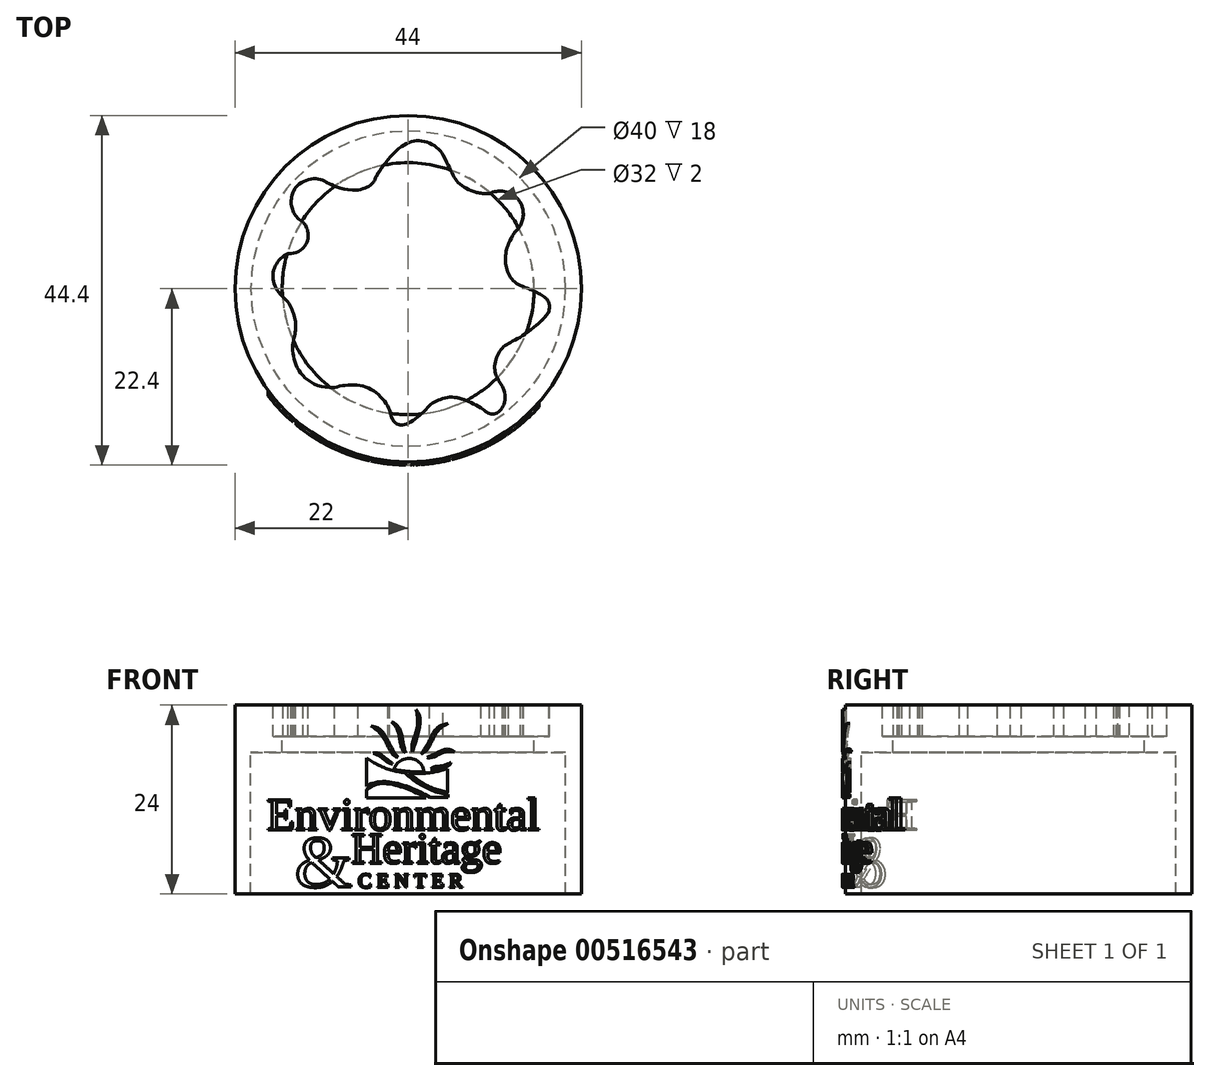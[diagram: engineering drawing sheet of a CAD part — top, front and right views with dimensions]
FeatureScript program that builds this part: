
annotation { "Feature Type Name" : "Feature", "Feature Type Description" : "" }
export const myFeature = defineFeature(function(context is Context, id is Id, definition is map)
    precondition{}
    {
        {
            var Q0;
            Q0=qCreatedBy(makeId("Top.planeOp"),FACE);
            var Q1;
            Q1=qBodyType(qCreatedBy(id+"F1",EDGE),BodyType.WIRE);
            cPlane(context, id + "F0", {"entities" : qUnion([Q0, Q1]), "cplaneType" : CPlaneType.OFFSET, "offset" : 12 * mm, "width" : 150 * mm, "height" : 150 * mm});
        }
        {
            var Q0;
            Q0=qCreatedBy(id+"F0.planeOp",FACE);
            var sketch = newSketch(context, id + "F1", { "sketchPlane" : qUnion([Q0])});
            skCircle(sketch, "E0", {"center": v(0, 0) * mm, "radius": 22 * mm});
            skFitSpline(sketch, "E1", {"points": [v(-14.3, 12.84) * mm, v(-11.44, 13.95) * mm, v(-6.4, 12.53) * mm], "startDerivative": vector(4.46, 5.6) * mm, "endDerivative": vector(16.32, 0.58) * mm});
            skFitSpline(sketch, "E2", {"points": [v(-14.3, 12.84) * mm, v(-14.8, 10.36) * mm, v(-13.38, 8.48) * mm], "startDerivative": vector(-2.91, -3.74) * mm, "endDerivative": vector(4.44, -2.3) * mm});
            skFitSpline(sketch, "E3", {"points": [v(-13.38, 8.48) * mm, v(-12.7, 6.62) * mm, v(-15.26, 4.45) * mm], "startDerivative": vector(2.5, -2.67) * mm, "endDerivative": vector(-9.07, 0.1) * mm});
            skFitSpline(sketch, "E4", {"points": [v(-15.26, 4.45) * mm, v(-17.17, 1.96) * mm, v(-15.87, -1.05) * mm], "startDerivative": vector(-5.88, -2.54) * mm, "endDerivative": vector(5.37, -3.99) * mm});
            skFitSpline(sketch, "E5", {"points": [v(-15.87, -1.05) * mm, v(-14.36, -3.98) * mm, v(-14.54, -6.45) * mm], "startDerivative": vector(4.6, -4.23) * mm, "endDerivative": vector(-1.12, -5.28) * mm});
            skFitSpline(sketch, "E6", {"points": [v(-14.54, -6.45) * mm, v(-14.3, -9.6) * mm, v(-9.38, -12.57) * mm], "startDerivative": vector(-1.49, -4.88) * mm, "endDerivative": vector(14.07, 0.6) * mm});
            skFitSpline(sketch, "E7", {"points": [v(-9.38, -12.57) * mm, v(-5.16, -12.57) * mm, v(-2.36, -15.43) * mm], "startDerivative": vector(7.18, 2.12) * mm, "endDerivative": vector(2.53, -6.19) * mm});
            skFitSpline(sketch, "E8", {"points": [v(-2.36, -15.43) * mm, v(-0.75, -17.32) * mm, v(2.7, -14.82) * mm], "startDerivative": vector(1.67, -9.42) * mm, "endDerivative": vector(5.03, 5.85) * mm});
            skFitSpline(sketch, "E9", {"points": [v(2.7, -14.82) * mm, v(5.45, -13.78) * mm, v(9.22, -15.14) * mm], "startDerivative": vector(4.06, 3.24) * mm, "endDerivative": vector(7.18, -3.93) * mm});
            skFitSpline(sketch, "E10", {"points": [v(9.22, -15.14) * mm, v(11.11, -15.85) * mm, v(12.13, -12.78) * mm], "startDerivative": vector(4.38, -3.77) * mm, "endDerivative": vector(-2.9, 8.35) * mm});
            skFitSpline(sketch, "E11", {"points": [v(12.13, -12.78) * mm, v(11.06, -10.66) * mm, v(11.96, -7.51) * mm], "startDerivative": vector(-1.65, 4.16) * mm, "endDerivative": vector(4.57, 5.25) * mm});
            skFitSpline(sketch, "E12", {"points": [v(11.96, -7.51) * mm, v(14.65, -5.88) * mm, v(17.91, -2.7) * mm], "startDerivative": vector(3.62, 3.57) * mm, "endDerivative": vector(-0.15, 3.1) * mm});
            skFitSpline(sketch, "E13", {"points": [v(17.91, -2.7) * mm, v(16.74, -0.7) * mm, v(14.28, 0.37) * mm], "startDerivative": vector(0.98, 7.59) * mm, "endDerivative": vector(-4.1, 1.2) * mm});
            skFitSpline(sketch, "E14", {"points": [v(14.28, 0.37) * mm, v(12.43, 2.83) * mm, v(12.74, 5.73) * mm], "startDerivative": vector(-6.41, 2.8) * mm, "endDerivative": vector(2.08, 5.38) * mm});
            skFitSpline(sketch, "E15", {"points": [v(12.74, 5.73) * mm, v(14.05, 7.73) * mm, v(14.57, 9.89) * mm], "startDerivative": vector(4.72, 10.1) * mm, "endDerivative": vector(-1.17, 4.74) * mm});
            skFitSpline(sketch, "E16", {"points": [v(14.57, 9.89) * mm, v(13.17, 12.02) * mm, v(10.32, 12.08) * mm], "startDerivative": vector(0.08, 3.85) * mm, "endDerivative": vector(-4.12, -2.28) * mm});
            skFitSpline(sketch, "E17", {"points": [v(10.32, 12.08) * mm, v(6.46, 13.4) * mm, v(4.44, 16.97) * mm], "startDerivative": vector(-9.93, -0.41) * mm, "endDerivative": vector(-5.62, 10.83) * mm});
            skFitSpline(sketch, "E18", {"points": [v(4.44, 16.97) * mm, v(1.52, 18.8) * mm, v(-2.58, 16.4) * mm], "startDerivative": vector(-2.9, 6.35) * mm, "endDerivative": vector(-8.38, -9.56) * mm});
            skFitSpline(sketch, "E19", {"points": [v(-2.58, 16.4) * mm, v(-4.36, 13.61) * mm, v(-6.4, 12.53) * mm], "startDerivative": vector(-9.43, -11.95) * mm, "endDerivative": vector(-8.2, -1.4) * mm});
            skCircle(sketch, "E20", {"center": v(0, 0) * mm, "radius": 20 * mm});
            skSolve(sketch);
        }
        {
            var Q0;
            Q0=qCreatedBy(makeId("Top.planeOp"),FACE);
            cPlane(context, id + "F2", {"entities" : qUnion([Q0]), "cplaneType" : CPlaneType.OFFSET, "offset" : 8 * mm, "width" : 150 * mm, "height" : 150 * mm});
        }
        {
            var Q0;
            Q0=qCreatedBy(id+"F2.planeOp",FACE);
            var sketch = newSketch(context, id + "F3", { "sketchPlane" : qUnion([Q0])});
            skCircle(sketch, "E21", {"center": v(0, 0) * mm, "radius": 20 * mm});
            skCircle(sketch, "E22", {"center": v(0, 0) * mm, "radius": 16 * mm});
            skSolve(sketch);
        }
        {
            var Q0;
            Q0=makeQuery(id+"F1.imprint","IMPRINT",FACE,{"disambiguationData":[TD([[makeQuery(id+"F1.imprint","IMPRINT",EDGE,{"derivedFrom":sQuery(id+"F1.wireOp",EDGE,"E1")}),1.0]])]});
            extrude(context, id + "F4", {"entities" : qUnion([Q0]), "oppositeDirection" : true, "depth" : 4 * mm});
        }
        {
            var Q0;
            Q0=makeQuery(id+"F1.imprint","IMPRINT",FACE,{"disambiguationData":[TD([[makeQuery(id+"F1.imprint","IMPRINT",EDGE,{"derivedFrom":sQuery(id+"F1.wireOp",EDGE,"E0")}),1.0]])]});
            extrude(context, id + "F5", {"entities" : qUnion([Q0]), "operationType" : NewBodyOperationType.ADD, "oppositeDirection" : true, "depth" : 24 * mm});
        }
        {
            var Q0;
            Q0=makeQuery(id+"F3.imprint","IMPRINT",FACE,{"disambiguationData":[TD([[makeQuery(id+"F3.imprint","IMPRINT",EDGE,{"derivedFrom":sQuery(id+"F3.wireOp",EDGE,"E21")}),1.0]])]});
            extrude(context, id + "F6", {"entities" : qUnion([Q0]), "operationType" : NewBodyOperationType.ADD, "oppositeDirection" : true, "depth" : 2 * mm});
        }
        {
            var Q0;
            Q0=qCreatedBy(id+"F0.planeOp",FACE);
            var sketch = newSketch(context, id + "F7", { "sketchPlane" : qUnion([Q0])});
            skCircle(sketch, "E23", {"center": v(0, 0) * mm, "radius": 22.4 * mm});
            skSolve(sketch);
        }
        {
            var Q0;
            Q0=qSketchRegion(id+"F7",true);
            var Q1;
            Q1=qConstructionFilter(qBodyType(qCreatedBy(id+"F7",EDGE),BodyType.WIRE),ConstructionObject.NO);
            extrude(context, id + "F8", {"entities" : qUnion([Q0]), "bodyType" : ToolBodyType.SURFACE, "operationType" : NewBodyOperationType.ADD, "surfaceEntities" : qUnion([Q1]), "oppositeDirection" : true, "depth" : 24 * mm});
        }
        {
            var Q0;
            Q0=qCreatedBy(makeId("Front.planeOp"),FACE);
            var sketch = newSketch(context, id + "F9", { "sketchPlane" : qUnion([Q0])});
            skText(sketch, "E24", { "text": "Environmental", "fontName": "Tinos-Regular.ttf"});
            skText(sketch, "E25", { "text": "Heritage", "fontName": "Tinos-Regular.ttf"});
            skText(sketch, "E26", { "text": "C E N T E R", "fontName": "Tinos-Regular.ttf"});
            skText(sketch, "E27", { "text": "&", "fontName": "Tinos-Regular.ttf"});
            skFitSpline(sketch, "E28", {"points": [v(0.99, 11.47) * mm, v(1.29, 8.55) * mm, v(0.58, 6.04) * mm], "startDerivative": vector(4.15, -4.4) * mm, "endDerivative": vector(-0.93, -4.32) * mm});
            skFitSpline(sketch, "E29", {"points": [v(0.99, 11.47) * mm, v(0.99, 8.58) * mm, v(0.58, 6.04) * mm], "startDerivative": vector(1.84, -7.67) * mm, "endDerivative": vector(1.86, -5.34) * mm});
            skFitSpline(sketch, "E30", {"points": [v(-2.14, 9.9) * mm, v(-0.8, 7.92) * mm, v(-0.37, 5.94) * mm], "startDerivative": vector(6.63, -2.68) * mm, "endDerivative": vector(1.8, -8.41) * mm});
            skFitSpline(sketch, "E31", {"points": [v(-2.14, 9.9) * mm, v(-1.12, 7.92) * mm, v(-0.37, 5.94) * mm], "startDerivative": vector(5.12, -5.44) * mm, "endDerivative": vector(3.25, -2.08) * mm});
            skFitSpline(sketch, "E32", {"points": [v(-4.7, 9.34) * mm, v(-2.58, 7.48) * mm, v(-1.32, 5.34) * mm], "startDerivative": vector(7.33, -0.56) * mm, "endDerivative": vector(3.4, -4.85) * mm});
            skFitSpline(sketch, "E33", {"points": [v(-4.7, 9.34) * mm, v(-2.86, 7.34) * mm, v(-1.32, 5.34) * mm], "startDerivative": vector(6.38, -4.28) * mm, "endDerivative": vector(4.77, -1.17) * mm});
            skFitSpline(sketch, "E34", {"points": [v(-4.44, 5.87) * mm, v(-2.99, 5.33) * mm, v(-1.97, 4.56) * mm], "startDerivative": vector(3.45, 1.25) * mm, "endDerivative": vector(1.98, -1.75) * mm});
            skFitSpline(sketch, "E35", {"points": [v(-4.44, 5.87) * mm, v(-3.14, 5.15) * mm, v(-1.97, 4.56) * mm], "startDerivative": vector(3.98, -1.43) * mm, "endDerivative": vector(2.3, 0.51) * mm});
            skFitSpline(sketch, "E36", {"points": [v(5.04, 9.66) * mm, v(2.81, 7.78) * mm, v(1.6, 5.74) * mm], "startDerivative": vector(-8.42, -0.62) * mm, "endDerivative": vector(-7.13, -11.13) * mm});
            skFitSpline(sketch, "E37", {"points": [v(1.6, 5.74) * mm, v(3.17, 7.74) * mm, v(5.04, 9.66) * mm], "startDerivative": vector(4.68, 1.67) * mm, "endDerivative": vector(6.71, 3.07) * mm});
            skFitSpline(sketch, "E38", {"points": [v(2.36, 5.33) * mm, v(3.9, 6.04) * mm, v(5.85, 6.08) * mm], "startDerivative": vector(3.07, 1.81) * mm, "endDerivative": vector(4.62, -3.5) * mm});
            skFitSpline(sketch, "E39", {"points": [v(2.36, 5.33) * mm, v(4.06, 5.8) * mm, v(5.85, 6.08) * mm], "startDerivative": vector(4.3, -0.66) * mm, "endDerivative": vector(6.53, -0.5) * mm});
            skFitSpline(sketch, "E40", {"points": [v(2.85, 3.87) * mm, v(4.24, 4.26) * mm, v(5.44, 4.7) * mm], "startDerivative": vector(2.8, 2.64) * mm, "endDerivative": vector(2.43, 0.94) * mm});
            skFitSpline(sketch, "E41", {"points": [v(2.85, 3.87) * mm, v(4.2, 4.01) * mm, v(5.44, 4.7) * mm], "startDerivative": vector(2.79, 0.01) * mm, "endDerivative": vector(1.38, 3.08) * mm});
            skFitSpline(sketch, "E42", {"points": [v(-5.32, 5.29) * mm, v(-2.85, 3.96) * mm, v(-0.38, 3.4) * mm], "startDerivative": vector(4.7, -2.94) * mm, "endDerivative": vector(5.12, -0.8) * mm});
            skFitSpline(sketch, "E43", {"points": [v(0.12, 3.36) * mm, v(2.71, 3.4) * mm, v(5, 3.92) * mm], "startDerivative": vector(5.14, -0.17) * mm, "endDerivative": vector(4.58, 1.28) * mm});
            skFitSpline(sketch, "E44", {"points": [v(-0.38, 3.4) * mm, v(2.1, 1.6) * mm, v(5.07, 0.67) * mm], "startDerivative": vector(4.45, -4.86) * mm, "endDerivative": vector(5.91, -0.41) * mm});
            skFitSpline(sketch, "E45", {"points": [v(0.12, 3.36) * mm, v(2.32, 1.8) * mm, v(5, 0.93) * mm], "startDerivative": vector(4.19, -3.44) * mm, "endDerivative": vector(5.54, -1.34) * mm});
            skFitSpline(sketch, "E46", {"points": [v(-1.82, 3.73) * mm, v(0.2, 5.23) * mm, v(2, 3.4) * mm], "startDerivative": vector(1.4, 5.98) * mm, "endDerivative": vector(-0.19, -6.24) * mm});
            skFitSpline(sketch, "E47", {"points": [v(-5.28, 1.68) * mm, v(-1.02, 1.95) * mm, v(2.8, 0.25) * mm], "startDerivative": vector(7.4, 5.13) * mm, "endDerivative": vector(7.35, -4.35) * mm});
            skFitSpline(sketch, "E48", {"points": [v(-5.29, 1.32) * mm, v(-1.13, 1.68) * mm, v(2.28, 0.24) * mm], "startDerivative": vector(8.31, 6.07) * mm, "endDerivative": vector(6.78, -3.82) * mm});
            skLineSegment(sketch, "E49", {"start": v(-5.32, 5.29) * mm, "end": v(-5.28, 1.68) * mm});
            skLineSegment(sketch, "E50", {"start": v(-5.29, 1.32) * mm, "end": v(-5.29, 0.24) * mm});
            skLineSegment(sketch, "E51", {"start": v(-5.29, 0.24) * mm, "end": v(2.28, 0.24) * mm});
            skLineSegment(sketch, "E52", {"start": v(5, 3.92) * mm, "end": v(5, 0.93) * mm});
            skLineSegment(sketch, "E53", {"start": v(2.8, 0.25) * mm, "end": v(5.07, 0.25) * mm});
            skLineSegment(sketch, "E54", {"start": v(5.07, 0.25) * mm, "end": v(5.07, 0.67) * mm});
            skFitSpline(sketch, "E55", {"points": [v(-1.8, 3.83) * mm, v(0, 3.56) * mm, v(2, 3.54) * mm], "startDerivative": vector(2.26, -0.6) * mm, "endDerivative": vector(4, 0.08) * mm});
            const initialGuessF9  = {"E24": [-0.01796, -0.00387, 1, 0, 0.0042], "E25": [-0.00726, -0.00808, 1, 0, 0.004], "E26": [-0.00637, -0.01118, 1, 0, 0.00186], "E27": [-0.0144, -0.0111, 1, 0, 0.00675]};
            skSetInitialGuess(sketch, initialGuessF9);
            skSolve(sketch);
        }
        {
            var Q0;
            Q0=qSketchRegion(id+"F9",true);
            var Q1;
            Q1=makeQuery(id+"F8.opExtrude","SWEPT_FACE",FACE,{"disambiguationData":[OSD([sQuery(id+"F7.wireOp",EDGE,"E23")])]});
            var Q2;
            Q2=makeQuery(id+"F5.opExtrude","SWEPT_FACE",FACE,{"disambiguationData":[OSD([sQuery(id+"F1.wireOp",EDGE,"E0")])]});
            extrude(context, id + "F10", {"entities" : qUnion([Q0]), "operationType" : NewBodyOperationType.ADD, "endBound" : BoundingType.UP_TO_SURFACE, "endBoundEntityFace" : qUnion([Q1]), "depth" : 25 * mm, "hasSecondDirection" : true, "secondDirectionBound" : SecondDirectionBoundingType.UP_TO_SURFACE, "secondDirectionOppositeDirection" : false, "secondDirectionBoundEntityFace" : qUnion([Q2]), "secondDirectionDepth" : 25 * mm, "offsetDistance" : 25 * mm});
        }
    });
